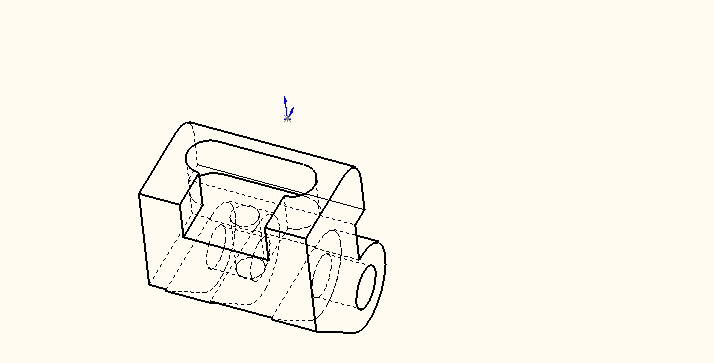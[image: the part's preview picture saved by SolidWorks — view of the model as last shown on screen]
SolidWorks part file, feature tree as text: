
SOLIDWORKS PART (.sldprt)
format: sldprt  version: not decoded by parser v0  size: 397,312 bytes
history: native  units: mm
features: sketch x6, cut_extrude x5, plane x2, material x1, extrude x1, fillet x1 (+11 scaffold rows collapsed)
feature tree (27):
  scaffold x11  (default folders/planes/origin — collapsed)
  material  "6061 Alloy"
  plane  "Plane1"  Offset=0mm
  sketch  "Sketch2"  dims[c1.D1=1.5875mm c1.D4=1.5875mm c1.D2=0.0mm c1.D3=0.0mm c1.D5=1.778mm c1.D6=0.0mm c1.D7=0.0mm c1.D8=0.762mm c1.D9=0.0mm c1.D10=~2.343632mm c2.D10=~68.853438deg c3.D10=~2.343632mm c4.D10=75.0deg c4.D11=3.81mm c4.D12=~6.539752mm c5.D12=135.0deg c5.D5=0.0mm c5.D10=1.27mm]
  extrude  "Extrude1"  Depth=0mm
  sketch  "Sketch8"  dims[D1=0.127mm]
  cut_extrude  "Cut-Extrude3"  [1 undecoded]
  plane  "Plane2"  Offset=3.429mm
  sketch  "Sketch5"  dims[D1=0.127mm D2=~4.130544mm]
  cut_extrude  "Cut-Extrude1"  Depth=2.286mm
  sketch  "Sketch7"
  cut_extrude  "Cut-Extrude2"  Depth=0.762mm
  sketch  "Sketch9"  dims[c1.D2=1.016mm c1.D1=1.524mm c1.D3=0.635mm c2.D1=1.905mm]
  cut_extrude  "Cut-Extrude4"  Depth=2.54mm
  sketch  "Sketch10"  dims[D1=~0.79375mm D2=3.175mm D3=3.175mm]
  cut_extrude  "Cut-Extrude5"  Depth=1.5875mm
  fillet  "Fillet1"  Radius=1.27mm
decode coverage: 11 of 13 modeling features carry decoded parameters
note: ~ marks probable driven/reference dimensions
note: 1 parameter value undecoded
note: suppression state not decoded; provenance and decode notes live in map.json
